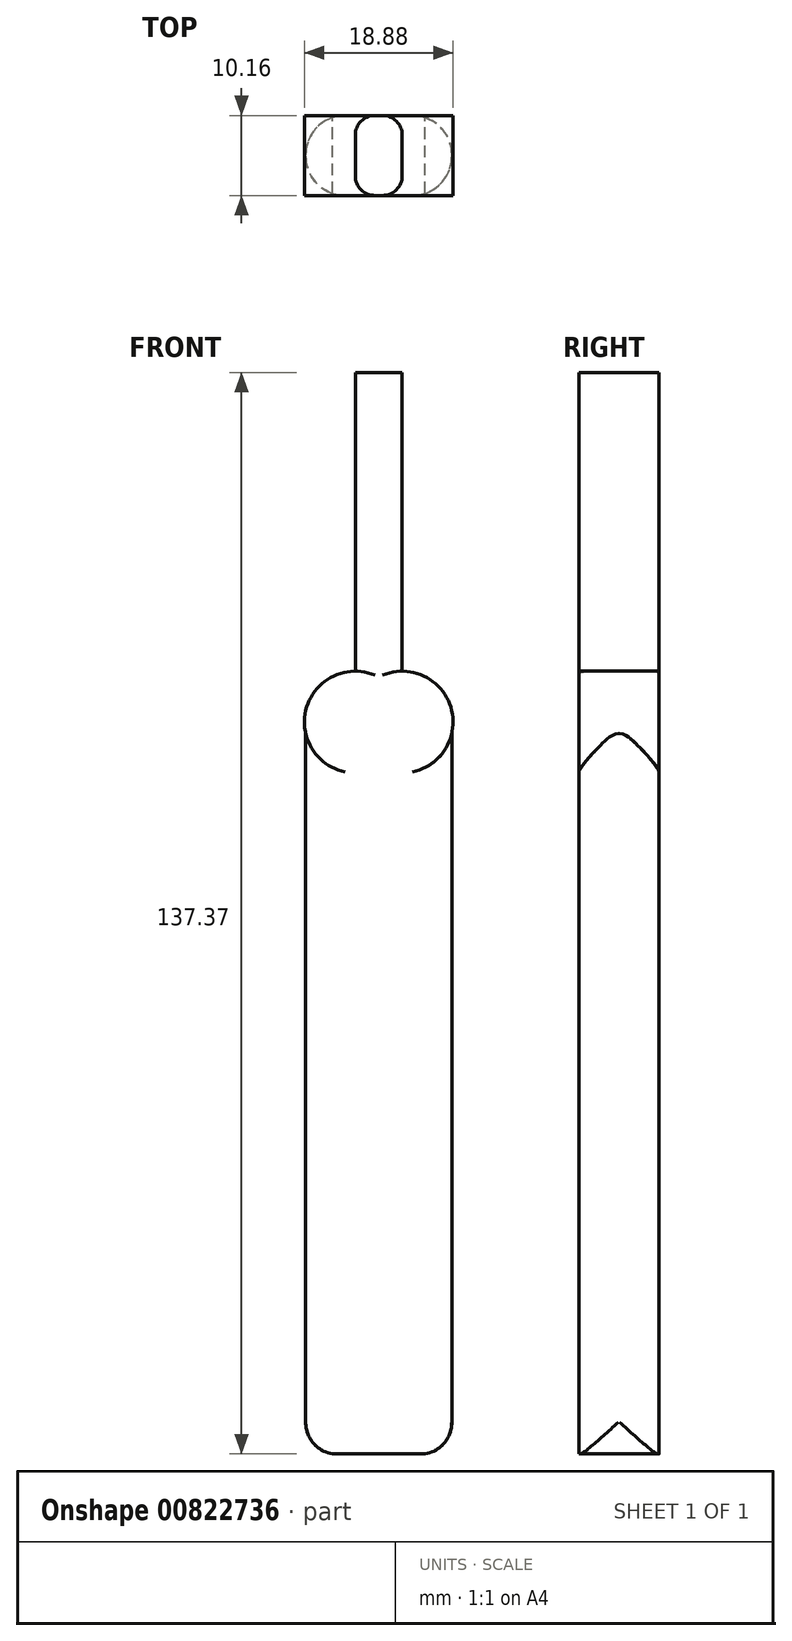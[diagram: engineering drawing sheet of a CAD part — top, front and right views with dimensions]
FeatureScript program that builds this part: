
annotation { "Feature Type Name" : "Feature", "Feature Type Description" : "" }
export const myFeature = defineFeature(function(context is Context, id is Id, definition is map)
    precondition{}
    {
        {
            var Q0;
            Q0=qCreatedBy(makeId("Front.planeOp"),FACE);
            var sketch = newSketch(context, id + "F0", { "sketchPlane" : qUnion([Q0])});
            skPoint(sketch, "E0.middle", {"position": v(0, 0) * mm});
            skLineSegment(sketch, "E1.left", {"start": v(-2.98, 50.8) * mm, "end": v(-2.98, 88.73) * mm});
            skPoint(sketch, "E1.middle", {"position": v(0, 69.77) * mm});
            skPoint(sketch, "E0.right.end.orphan", {"position": v(-9.28, 50.8) * mm});
            skArc(sketch, "E2", {"start": v(-2.98, 50.8) * mm, "mid": v(-8.04, 48.36) * mm, "end": v(-9.28, 42.89) * mm});
            skLineSegment(sketch, "E3", {"start": v(-9.28, 42.89) * mm, "end": v(-9.28, -44.62) * mm});
            skArc(sketch, "E4", {"start": v(-9.28, -44.62) * mm, "mid": v(-8.31, -47.25) * mm, "end": v(-5.87, -48.64) * mm});
            skLineSegment(sketch, "E5", {"start": v(-5.87, -48.64) * mm, "end": v(0, -48.64) * mm});
            skPoint(sketch, "E1.top.end.orphan", {"position": v(2.98, 88.73) * mm});
            skPoint(sketch, "E1.bottom.end.orphan", {"position": v(2.98, 50.8) * mm});
            skLineSegment(sketch, "E6.MirrorCS", {"start": v(9.28, 42.89) * mm, "end": v(9.28, -44.62) * mm});
            skArc(sketch, "E7.MirrorCS", {"start": v(9.28, -44.62) * mm, "mid": v(8.31, -47.25) * mm, "end": v(5.87, -48.64) * mm});
            skLineSegment(sketch, "E8.MirrorCS", {"start": v(5.87, -48.64) * mm, "end": v(0, -48.64) * mm});
            skArc(sketch, "E9.MirrorCS", {"start": v(2.98, 50.8) * mm, "mid": v(8.04, 48.36) * mm, "end": v(9.28, 42.89) * mm});
            skLineSegment(sketch, "E10.MirrorCS", {"start": v(2.98, 50.8) * mm, "end": v(2.98, 88.73) * mm});
            skPoint(sketch, "E11.end.orphan", {"position": v(0, 88.73) * mm});
            skLineSegment(sketch, "E12", {"start": v(-2.98, 88.73) * mm, "end": v(2.98, 88.73) * mm});
            skSolve(sketch);
        }
        {
            var Q0;
            Q0 = qSketchRegion(id + "F0", true);
            extrude(context, id + "F1", {"entities" : qUnion([Q0]), "depth" : 10.16 * mm, "offsetDistance" : 25 * mm});
        }
        {
            var Q0;
            Q0=makeQuery(id+"F1.opExtrude","CAP_EDGE",EDGE,{"disambiguationData":[OSD([sQuery(id+"F0.wireOp",EDGE,"E1.left")])],"isStart":true});
            var Q1;
            Q1=makeQuery(id+"F1.opExtrude","CAP_EDGE",EDGE,{"disambiguationData":[OSD([sQuery(id+"F0.wireOp",EDGE,"E10.MirrorCS")])],"isStart":false});
            var Q2;
            Q2=makeQuery(id+"F1.opExtrude","CAP_EDGE",EDGE,{"disambiguationData":[OSD([sQuery(id+"F0.wireOp",EDGE,"E1.left")])],"isStart":false});
            var Q3;
            Q3=makeQuery(id+"F1.opExtrude","CAP_EDGE",EDGE,{"disambiguationData":[OSD([sQuery(id+"F0.wireOp",EDGE,"E10.MirrorCS")])],"isStart":true});
            fillet(context, id + "F2", {"entities" : qUnion([Q0, Q1, Q2, Q3]), "radius" : 2.5 * mm, "tangentPropagation" : true, "allowEdgeOverflow" : false});
        }
        {
            var Q0;
            Q0=makeQuery(id+"F1.opExtrude","CAP_EDGE",EDGE,{"disambiguationData":[OSD([sQuery(id+"F0.wireOp",EDGE,"E3")])],"isStart":true});
            var Q1;
            Q1=makeQuery(id+"F1.opExtrude","CAP_EDGE",EDGE,{"disambiguationData":[OSD([sQuery(id+"F0.wireOp",EDGE,"E6.MirrorCS")])],"isStart":true});
            var Q2;
            Q2=makeQuery(id+"F1.opExtrude","CAP_EDGE",EDGE,{"disambiguationData":[OSD([sQuery(id+"F0.wireOp",EDGE,"E3")])],"isStart":false});
            var Q3;
            Q3=makeQuery(id+"F1.opExtrude","CAP_EDGE",EDGE,{"disambiguationData":[OSD([sQuery(id+"F0.wireOp",EDGE,"E6.MirrorCS")])],"isStart":false});
            fillet(context, id + "F3", {"entities" : qUnion([Q0, Q1, Q2, Q3]), "radius" : 5 * mm, "tangentPropagation" : true, "allowEdgeOverflow" : false});
        }
    });
